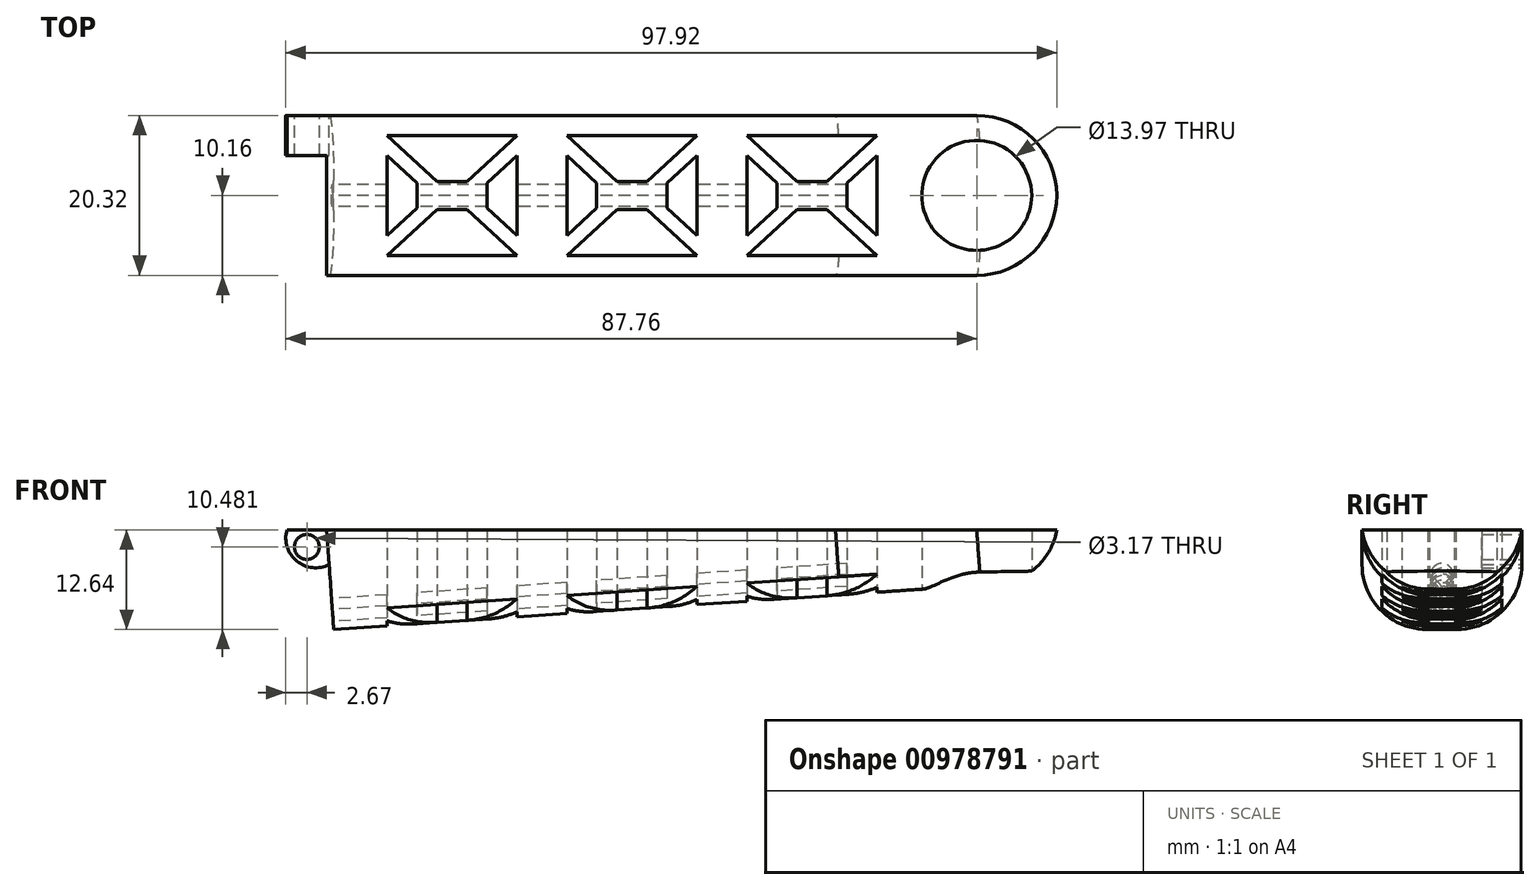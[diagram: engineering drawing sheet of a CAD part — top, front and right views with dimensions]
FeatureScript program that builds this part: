
annotation { "Feature Type Name" : "Feature", "Feature Type Description" : "" }
export const myFeature = defineFeature(function(context is Context, id is Id, definition is map)
    precondition{}
    {
        {
            var Q0;
            Q0=qCreatedBy(makeId("Top.planeOp"),FACE);
            var sketch = newSketch(context, id + "F0", { "sketchPlane" : qUnion([Q0])});
            skCircle(sketch, "E0", {"center": v(0, 0) * mm, "radius": 6.99 * mm});
            skArc(sketch, "E1", {"start": v(0, -10.16) * mm, "mid": v(10.16, 0) * mm, "end": v(0, 10.16) * mm});
            skLineSegment(sketch, "E2", {"start": v(0, 10.16) * mm, "end": v(-82.55, 10.16) * mm});
            skLineSegment(sketch, "E3", {"start": v(0, -10.16) * mm, "end": v(-82.55, -10.16) * mm});
            skLineSegment(sketch, "E4", {"start": v(-82.55, 10.16) * mm, "end": v(-82.55, -10.16) * mm});
            skLineSegment(sketch, "E5", {"start": v(-29.21, 7.62) * mm, "end": v(-12.7, 7.62) * mm});
            skLineSegment(sketch, "E6", {"start": v(-12.7, 7.62) * mm, "end": v(-19.05, 1.78) * mm});
            skLineSegment(sketch, "E7", {"start": v(-19.05, 1.78) * mm, "end": v(-22.86, 1.78) * mm});
            skLineSegment(sketch, "E8", {"start": v(-22.86, 1.78) * mm, "end": v(-29.21, 7.62) * mm});
            skLineSegment(sketch, "E9", {"start": v(0, 0) * mm, "end": v(-42.97, 0) * mm});
            skLineSegment(sketch, "E10.MirrorCS", {"start": v(-19.05, -1.78) * mm, "end": v(-22.86, -1.78) * mm});
            skLineSegment(sketch, "E11.MirrorCS", {"start": v(-22.86, -1.78) * mm, "end": v(-29.21, -7.62) * mm});
            skLineSegment(sketch, "E12.MirrorCS", {"start": v(-29.21, -7.62) * mm, "end": v(-12.7, -7.62) * mm});
            skLineSegment(sketch, "E13.MirrorCS", {"start": v(-12.7, -7.62) * mm, "end": v(-19.05, -1.78) * mm});
            skLineSegment(sketch, "E14", {"start": v(-16.51, 1.57) * mm, "end": v(-16.51, -1.57) * mm});
            skLineSegment(sketch, "E15", {"start": v(-16.51, -1.57) * mm, "end": v(-12.7, -5.08) * mm});
            skLineSegment(sketch, "E16", {"start": v(-12.7, -5.08) * mm, "end": v(-12.7, 5.08) * mm});
            skLineSegment(sketch, "E17", {"start": v(-12.7, 5.08) * mm, "end": v(-16.5, 1.57) * mm});
            skLineSegment(sketch, "E18", {"start": v(-20.96, 1.78) * mm, "end": v(-20.96, 3.6) * mm});
            skLineSegment(sketch, "E19.MirrorCS", {"start": v(-25.4, 1.57) * mm, "end": v(-25.4, -1.57) * mm});
            skLineSegment(sketch, "E20.MirrorCS", {"start": v(-29.21, 5.08) * mm, "end": v(-25.4, 1.57) * mm});
            skLineSegment(sketch, "E21.MirrorCS", {"start": v(-29.21, -5.08) * mm, "end": v(-29.21, 5.08) * mm});
            skLineSegment(sketch, "E22.MirrorCS", {"start": v(-25.4, -1.57) * mm, "end": v(-29.21, -5.08) * mm});
            skLineSegment(sketch, "E23.1.0.0", {"start": v(-52.07, 5.08) * mm, "end": v(-48.26, 1.57) * mm});
            skLineSegment(sketch, "E23.1.0.1", {"start": v(-52.07, -7.62) * mm, "end": v(-35.56, -7.62) * mm});
            skLineSegment(sketch, "E23.1.0.2", {"start": v(-52.07, -5.08) * mm, "end": v(-52.07, 5.08) * mm});
            skLineSegment(sketch, "E23.1.0.3", {"start": v(-35.56, -5.08) * mm, "end": v(-35.56, 5.08) * mm});
            skLineSegment(sketch, "E23.1.0.4", {"start": v(-48.26, 1.57) * mm, "end": v(-48.26, -1.57) * mm});
            skLineSegment(sketch, "E23.1.0.5", {"start": v(-52.07, 7.62) * mm, "end": v(-35.56, 7.62) * mm});
            skLineSegment(sketch, "E23.1.0.6", {"start": v(-41.91, 1.78) * mm, "end": v(-45.72, 1.78) * mm});
            skLineSegment(sketch, "E23.1.0.7", {"start": v(-48.26, -1.57) * mm, "end": v(-52.07, -5.08) * mm});
            skLineSegment(sketch, "E23.1.0.8", {"start": v(-35.56, 7.62) * mm, "end": v(-41.9, 1.78) * mm});
            skLineSegment(sketch, "E23.1.0.9", {"start": v(-45.72, -1.78) * mm, "end": v(-52.07, -7.62) * mm});
            skLineSegment(sketch, "E23.1.0.10", {"start": v(-39.37, -1.57) * mm, "end": v(-35.56, -5.08) * mm});
            skLineSegment(sketch, "E23.1.0.11", {"start": v(-45.72, 1.78) * mm, "end": v(-52.07, 7.62) * mm});
            skLineSegment(sketch, "E23.1.0.12", {"start": v(-39.37, 1.57) * mm, "end": v(-39.37, -1.57) * mm});
            skLineSegment(sketch, "E23.1.0.13", {"start": v(-35.56, 5.08) * mm, "end": v(-39.37, 1.57) * mm});
            skLineSegment(sketch, "E23.1.0.14", {"start": v(-43.81, 1.78) * mm, "end": v(-43.81, 3.6) * mm});
            skLineSegment(sketch, "E23.1.0.15", {"start": v(-35.56, -7.62) * mm, "end": v(-41.91, -1.78) * mm});
            skLineSegment(sketch, "E23.1.0.16", {"start": v(-41.91, -1.78) * mm, "end": v(-45.72, -1.78) * mm});
            skLineSegment(sketch, "E23.2.0.0", {"start": v(-74.93, 5.08) * mm, "end": v(-71.12, 1.57) * mm});
            skLineSegment(sketch, "E23.2.0.1", {"start": v(-74.93, -7.62) * mm, "end": v(-58.42, -7.62) * mm});
            skLineSegment(sketch, "E23.2.0.2", {"start": v(-74.93, -5.08) * mm, "end": v(-74.93, 5.08) * mm});
            skLineSegment(sketch, "E23.2.0.3", {"start": v(-58.42, -5.08) * mm, "end": v(-58.42, 5.08) * mm});
            skLineSegment(sketch, "E23.2.0.4", {"start": v(-71.12, 1.57) * mm, "end": v(-71.12, -1.57) * mm});
            skLineSegment(sketch, "E23.2.0.5", {"start": v(-74.93, 7.62) * mm, "end": v(-58.42, 7.62) * mm});
            skLineSegment(sketch, "E23.2.0.6", {"start": v(-64.77, 1.78) * mm, "end": v(-68.58, 1.78) * mm});
            skLineSegment(sketch, "E23.2.0.7", {"start": v(-71.12, -1.57) * mm, "end": v(-74.93, -5.08) * mm});
            skLineSegment(sketch, "E23.2.0.8", {"start": v(-58.42, 7.62) * mm, "end": v(-64.77, 1.78) * mm});
            skLineSegment(sketch, "E23.2.0.9", {"start": v(-68.58, -1.78) * mm, "end": v(-74.93, -7.62) * mm});
            skLineSegment(sketch, "E23.2.0.10", {"start": v(-62.23, -1.57) * mm, "end": v(-58.42, -5.08) * mm});
            skLineSegment(sketch, "E23.2.0.11", {"start": v(-68.58, 1.78) * mm, "end": v(-74.93, 7.62) * mm});
            skLineSegment(sketch, "E23.2.0.12", {"start": v(-62.23, 1.57) * mm, "end": v(-62.23, -1.57) * mm});
            skLineSegment(sketch, "E23.2.0.13", {"start": v(-58.42, 5.08) * mm, "end": v(-62.23, 1.57) * mm});
            skLineSegment(sketch, "E23.2.0.14", {"start": v(-66.67, 1.78) * mm, "end": v(-66.67, 3.6) * mm});
            skLineSegment(sketch, "E23.2.0.15", {"start": v(-58.42, -7.62) * mm, "end": v(-64.77, -1.78) * mm});
            skLineSegment(sketch, "E23.2.0.16", {"start": v(-64.77, -1.78) * mm, "end": v(-68.58, -1.78) * mm});
            skLineSegment(sketch, "E23.direction1", {"start": v(-29.21, -7.62) * mm, "end": v(-52.07, -7.62) * mm, "construction": true});
            skSolve(sketch);
        }
        {
            var Q0;
            Q0 = qSketchRegion(id + "F0", true);
            extrude(context, id + "F1", {"entities" : qUnion([Q0]), "depth" : 12.7 * mm, "offsetDistance" : 25.4 * mm});
        }
        {
            var Q0;
            Q0=makeQuery(id+"F1.opExtrude","SWEPT_FACE",FACE,{"disambiguationData":[OSD([sQuery(id+"F0.wireOp",EDGE,"E3")])]});
            var sketch = newSketch(context, id + "F2", { "sketchPlane" : qUnion([Q0])});
            skLineSegment(sketch, "E24", {"start": v(10.16, 12.7) * mm, "end": v(10.16, 0) * mm});
            skLineSegment(sketch, "E25.0", {"start": v(0, 0) * mm, "end": v(10.16, 0) * mm});
            skLineSegment(sketch, "E26.0", {"start": v(0, 0) * mm, "end": v(-82.55, 0) * mm});
            skLineSegment(sketch, "E27", {"start": v(-82.55, 0) * mm, "end": v(10.16, 6.35) * mm});
            skSolve(sketch);
        }
        {
            var Q0;
            Q0 = qSketchRegion(id + "F2", true);
            extrude(context, id + "F3", {"entities" : qUnion([Q0]), "operationType" : NewBodyOperationType.REMOVE, "endBound" : BoundingType.SYMMETRIC, "oppositeDirection" : true, "depth" : 50.8 * mm, "offsetDistance" : 25.4 * mm});
        }
        {
            var Q0;
            Q0=makeQuery(id+"F3.boolean.opBoolean","INTERSECT",EDGE,{"derivedFrom":[makeQuery(id+"F1.opExtrude","SWEPT_FACE",FACE,{"disambiguationData":[OSD([sQuery(id+"F0.wireOp",EDGE,"E2")])]}),makeQuery(id+"F3.opExtrude","SWEPT_FACE",FACE,{"disambiguationData":[OSD([sQuery(id+"F2.wireOp",EDGE,"E27")])]})]});
            var Q1;
            Q1=makeQuery(id+"F3.boolean.opBoolean","INTERSECT",EDGE,{"derivedFrom":[makeQuery(id+"F1.opExtrude","SWEPT_FACE",FACE,{"disambiguationData":[OSD([sQuery(id+"F0.wireOp",EDGE,"E3")])]}),makeQuery(id+"F3.opExtrude","SWEPT_FACE",FACE,{"disambiguationData":[OSD([sQuery(id+"F2.wireOp",EDGE,"E27")])]})]});
            var Q2;
            Q2=makeQuery(id+"F3.boolean.opBoolean","INTERSECT",EDGE,{"derivedFrom":[makeQuery(id+"F1.opExtrude","SWEPT_FACE",FACE,{"disambiguationData":[OSD([sQuery(id+"F0.wireOp",EDGE,"E1")])]}),makeQuery(id+"F3.opExtrude","SWEPT_FACE",FACE,{"disambiguationData":[OSD([sQuery(id+"F2.wireOp",EDGE,"E27")])]})]});
            fillet(context, id + "F4", {"entities" : qUnion([Q0, Q1, Q2]), "radius" : 8.25 * mm, "tangentPropagation" : true, "allowEdgeOverflow" : false});
        }
        {
            var Q0;
            Q0=makeQuery(id+"F1.opExtrude","SWEPT_FACE",FACE,{"disambiguationData":[OSD([sQuery(id+"F0.wireOp",EDGE,"E3")])]});
            var sketch = newSketch(context, id + "F5", { "sketchPlane" : qUnion([Q0])});
            skLineSegment(sketch, "E28", {"start": v(-82.55, 12.7) * mm, "end": v(-82.55, 0) * mm});
            skLineSegment(sketch, "E29", {"start": v(-82.55, 12.7) * mm, "end": v(-81.68, 0) * mm});
            skLineSegment(sketch, "E30", {"start": v(-81.68, 0) * mm, "end": v(-82.55, 0) * mm});
            skSolve(sketch);
        }
        {
            var Q0;
            Q0 = qSketchRegion(id + "F5", true);
            extrude(context, id + "F6", {"entities" : qUnion([Q0]), "operationType" : NewBodyOperationType.REMOVE, "oppositeDirection" : true, "depth" : 25.4 * mm, "offsetDistance" : 25.4 * mm});
        }
        {
            var Q0;
            Q0=makeQuery(id+"F6.boolean.opBoolean","COPY",FACE,{"derivedFrom":makeQuery(id+"F6.opExtrude","SWEPT_FACE",FACE,{"disambiguationData":[OSD([sQuery(id+"F5.wireOp",EDGE,"E29")])]})});
            var sketch = newSketch(context, id + "F7", { "sketchPlane" : qUnion([Q0])});
            skArc(sketch, "E31", {"start": v(1.4, 8.18) * mm, "mid": v(0, 9.58) * mm, "end": v(-1.4, 8.18) * mm});
            skPoint(sketch, "E31.centerSnap0", {"position": v(0, 5.64) * mm});
            skLineSegment(sketch, "E32", {"start": v(1.4, 8.18) * mm, "end": v(0, 6.66) * mm});
            skLineSegment(sketch, "E33", {"start": v(0, 6.66) * mm, "end": v(-1.4, 8.18) * mm});
            skSolve(sketch);
        }
        {
            var Q0;
            Q0 = qSketchRegion(id + "F7", true);
            extrude(context, id + "F8", {"entities" : qUnion([Q0]), "operationType" : NewBodyOperationType.REMOVE, "oppositeDirection" : true, "depth" : 67.56 * mm, "offsetDistance" : 25.4 * mm});
        }
        {
            var Q0;
            Q0=makeQuery(id+"F1.opExtrude","SWEPT_FACE",FACE,{"disambiguationData":[OSD([sQuery(id+"F0.wireOp",EDGE,"E2")])]});
            var sketch = newSketch(context, id + "F9", { "sketchPlane" : qUnion([Q0])});
            skLineSegment(sketch, "E34", {"start": v(82.55, 12.7) * mm, "end": v(82.25, 8.3) * mm});
            skLineSegment(sketch, "E35", {"start": v(82.55, 12.7) * mm, "end": v(87.63, 12.7) * mm});
            skCircle(sketch, "E36", {"center": v(85.1, 10.54) * mm, "radius": 1.59 * mm});
            skPoint(sketch, "E36.centerSnap0", {"position": v(85.1, 12.7) * mm});
            skLineSegment(sketch, "E37.0", {"start": v(17.94, 12.7) * mm, "end": v(82.25, 8.3) * mm});
            skArc(sketch, "E38", {"start": v(82.25, 8.3) * mm, "mid": v(86.37, 8.75) * mm, "end": v(87.63, 12.7) * mm});
            skSolve(sketch);
        }
        {
            var Q0;
            Q0 = qSketchRegion(id + "F9", true);
            extrude(context, id + "F10", {"entities" : qUnion([Q0]), "operationType" : NewBodyOperationType.ADD, "oppositeDirection" : true, "depth" : 5.08 * mm, "offsetDistance" : 25.4 * mm});
        }
    });
